# Revit family: NBS_DudleyIndustriesLimited_SoapDpnsrs_ClassicBehindTheMirrorRangePullDownSoapDispenser2L
name_source: partatom
category: Specialty Equipment
units: mm (PartAtom-declared; Revit-internal decimal feet)

## family parameters
Cut with Voids When Loaded = No
Host = Face
Part Type = Normal
Room Calculation Point = No
Round Connector Dimension = Use Diameter
Shared = No

## types (1)
- ClassicBehindTheMirrorPullDownSoapDispenser
    AssetType = Fixed
    BIMObjectName = NBS_DudleyIndustriesLimited_SoapDispensers_ClassicBehindTheMirrorPullDownSoapDispenser
    Category = Pr_40_70_22_81:Soap dispensers
    ClearanceZoneMaterial = NBS_ClearanceZone
    Color = Silver
    CountryOfMaterialOrigin = United Kingdom
    CountryOfProductManufacture = United Kingdom
    Default Elevation = 0 mm  [stored 0 ft]
    Description = Innovative touch-free soap dispenser with large capacity, for discrete installation behind a mirror in  bespoke cabinets
    DispenserMaterial = NBS_DudleyIndustriesLimited_StainlessSteel_Brushed
    DurationUnit = year
    Features = Large 2L capacity touch free soap dispenser ideal for busy washrooms, holds enough soap for 3,200 dispenses, co-ordinating paper towel dispenser also available, the dispenser is fixed into place using 4 base panel fixings
    Finish = Other
    Fixings = Four base panel fixings
    Form = Wall-mounted
    IfcExportAs = IfcFurnitureType
    IfcExportType = USERDEFINED
    ManufacturerName = Dudley Industries Limited
    ManufacturerURL = www.dudleyindustries.com
    Material = Stainless steel
    MaterialsBody = Stainless steel
    MaterialsFinishAndColour = Silver
    ModelNumber = 92071SS
    ModelReference = Classic Behind the Mirror Pull Down Soap Dispenser
    NBSInstanceId = e0e5ac9a-4faa-4012-b200-953b3cbb91c4
    NBSObjectId = c9daa17d-ce92-4d6b-ba07-9e8aca8b75eb
    NBSVariantId = 00000000-0000-0000-0000-000000000000
    Name = SoapDispensers_ClassicBehindTheMirrorPullDownSoapDispenser_DudleyIndustriesLimited
    NominalHeight = 353 mm  [stored 1.15814 ft]
    NominalLength = 195 mm  [stored 0.639764 ft]
    NominalWidth = 228 mm  [stored 0.748031 ft]
    Operation = Pull-down
    ProductInformation = https://source.thenbs.com
    Shape = Rectangle
    Size = 353 x 228 x 195 mm
    Uniclass2015Code = Pr_40_70_22_81
    Uniclass2015Title = Soap dispensers
    Uniclass2015Version = Products v1.30
    Version = 2
    WarrantyDescription = Ten year
    WarrantyDurationUnit = year

note: [stored X ft] marks values corroborated as IEEE doubles in the binary element streams (Revit-internal decimal feet)

## geometry (parser evidence)
native form markers: Sweep x2
no freeform markers — native parametric forms only
